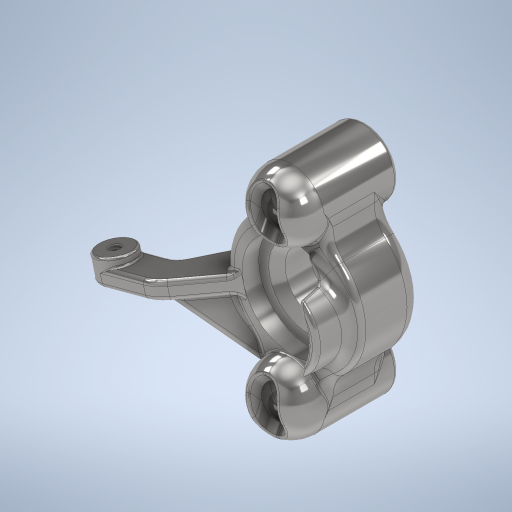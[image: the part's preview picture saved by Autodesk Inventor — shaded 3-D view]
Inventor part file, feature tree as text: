
AUTODESK INVENTOR PART (.ipt)
format: ipt  version: 2024 (Build 280153000, 153)  size: 1,564,160 bytes
history: native  units: in
note: dims shown in document units (in); Inventor stores cm internally (conversion verified against a paired STEP export)
features: fillet x21, sketch x14, extrude x9, projected_geometry x6, plane x4, revolve x3, thread x3, other x3, chamfer x2, mirror x1, hole x1, rib x1, draft x1
ambient origin geometry x8: Origin, YZ Plane, XZ Plane, XY Plane, X Axis, Y Axis, Z Axis, Center Point
bodies: Solid1 (feature_tree)
feature tree (69):
  extrude  "Extrusion1"  Depth=0.5in
  fillet  "Fillet1"  Radius=0.5in
  revolve  "Revolution1"  [1 undecoded]
  mirror  "Mirror1"
  extrude  "Extrusion2"  TaperAngle=90.0deg  [1 undecoded]
  extrude  "Extrusion3"  Depth=0.125in TaperAngle=0.0deg
  plane  "Work Plane1"
  plane  "Work Plane3"
  extrude  "Extrusion4"  Depth=0.1875in TaperAngle=0.0deg
  revolve  "Revolution2"  Angle=15.0deg
  revolve  "Revolution3"  [1 undecoded]
  fillet  "Fillet2"  Radius=0.215in
  extrude  "Extrusion5"  Depth=0.215in
  chamfer  "Chamfer1"  Distance=0.0625in
  extrude  "Extrusion6"  Depth=0.475in
  fillet  "Fillet3"  [1 undecoded]
  fillet  "Fillet4"  Radius=0.015in
  fillet  "Fillet5"  Radius=0.0625in
  fillet  "Fillet6"  Radius=0.015in
  chamfer  "Chamfer2"  Distance=0.0625in Angle=45.0deg
  thread  "Thread1"  [1 undecoded]
  thread  "Thread2"  [1 undecoded]
  thread  "Thread3"  [1 undecoded]
  fillet  "Fillet7"  Radius=0.125in
  fillet  "Fillet8"  Radius=0.032in
  fillet  "Fillet9"  Radius=0.032in
  extrude  "Extrusion7"  Depth=1.2in
  fillet  "Fillet10"  Radius=0.135in
  fillet  "Fillet11"  Radius=0.15in
  fillet  "Fillet12"  [1 undecoded]
  extrude  "Extrusion8"  Depth=0.032in
  fillet  "Fillet13"  Radius=0.25in
  hole  "Hole2"  [1 undecoded]
  fillet  "Fillet14"  Radius=0.0625in
  plane  "Work Plane4"
  rib  "Rib1"
  fillet  "Fillet15"  Radius=0.032in
  fillet  "Fillet16"  Radius=0.015in
  extrude  "Extrusion9"  Depth=0.1in
  draft  "FaceDraft1"
  fillet  "Fillet17"  Radius=0.05in
  fillet  "Fillet18"  Radius=0.05in
  fillet  "Fillet19"  Radius=0.315in
  fillet  "Fillet20"  Radius=0.25in
  fillet  "Fillet21"  Radius=0.0172in
  sketch  "Sketch1"  dims[d0=1.7625in d1=0.5in d2=0.5in]
  sketch  "Sketch2"  dims[d3=0.5625in d4=0.0in d5=0.25in]
  sketch  "Sketch3"  dims[d6=0.325in d7=90.0deg]
  sketch  "Sketch4"  dims[d8=0.75in d9=0.125in d10=0.0in]
  other  "Work Axis1"
  other  "Work Axis2"
  plane  "Work Plane2"
  other  "Work Axis3"
  sketch  "Sketch5"  dims[d11=0.5in d12=0.1875in d13=0.0in]
  sketch  "Sketch6"  dims[d14=15.0deg d15=15.0deg]
  sketch  "Sketch7"  dims[d16=0.0in d17=0.0in d18=0.0in d19=0.215in]
  sketch  "Sketch8"  dims[d20=0.6871in d21=0.215in]
  sketch  "Sketch9"  dims[d22=0.6871in]
  sketch  "Sketch10"  dims[d23=0.1in d24=0.0625in d25=0.0in]
  sketch  "Sketch11"  dims[d26=0.015in d27=0.125in d28=45.0deg d29=0.475in d30=0.0in d31=0.0in d32=0.015in d33=0.0625in d34=0.015in]
  sketch  "Sketch13"  dims[d35=0.014in d36=0.0625in d37=0.125in d38=45.0deg d39=0.315in d40=0.0in d41=0.315in d42=0.0in d43=0.315in d44=0.0in d45=0.125in d46=0.032in d47=0.032in]
  sketch  "Sketch14"  dims[d48=0.3779in d52=1.2in d53=0.135in d54=0.15in d55=15.0deg]
  sketch  "Sketch15"  dims[d56=0.125in d57=0.0in d58=0.032in d59=0.25in d60=0.125in d61=0.0625in d62=0.0in d63=0.032in d71=0.0849in d72=0.75in d73=0.2362in d74=0.1181in d75=0.5635in d76=0.75in d77=0.8108in d78=0.015in d79=0.1in d80=0.1in d81=0.0in d82=0.0in d83=0.1in d84=0.1in d85=0.05in d86=0.05in d87=0.315in d88=0.25in d89=0.0in d90=0.0172in d91=0.125in d92=0.032in d93=0.015in d94=0.015in d95=0.015in d64=1.0in d65=1.0in d66=1.0in d67=0.15in d68=0.25in d69=0.375in d70=0.5635in d96=0.0in]
  projected_geometry  "Project Cut Edges1"
  projected_geometry  "Project Cut Edges2"
  projected_geometry  "Project Cut Edges3"
  projected_geometry  "Project Cut Edges4"
  projected_geometry  "Project Cut Edges5"
  projected_geometry  "Project Cut Edges6"
note: 9 required parameter values undecoded (feature->parameter linkage not recoverable at this tier; creation-order binding heuristic only, values carry confidence <= 0.55)